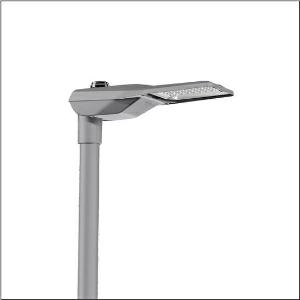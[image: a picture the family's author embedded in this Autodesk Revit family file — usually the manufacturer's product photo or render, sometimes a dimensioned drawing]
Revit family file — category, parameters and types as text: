
# Revit family: streetlight_sl_21_mini___st0_8a_5xe6c37n08gb_efcc
name_source: partatom
category: Lighting Fixtures
units: mm (PartAtom-declared; Revit-internal decimal feet)

## family parameters
Cut with Voids When Loaded = No
Host = Face
Light Source = No
Part Type = Normal
Room Calculation Point = No
Round Connector Dimension = Use Diameter
Shared = No

## types (1)
- --- (1 x LED, 5940 lm, 40.4 W, 3000K)
    Apparent Load = 40 VA
    CIE Flux Codes = 38 75 97 100 100
    Color Rendering = 70
    Color Temperature = 3000K
    Default Elevation = 1800 mm
    Description = Streetlight SL 21 mini, mast luminaire, primary light control with lens, of PMMA, primary optical cover: cover, of toughened safety glass, transparent, light distribution: ST0.8a, light emission: direct distribution, primary light characteristic: asymmetric, installation type: side-entry, LED, 3G 1.5mm², High Power LED, rated luminous flux: 5.940lm, luminous efficacy: 147lm/W, light colour: 730, colour temperature: 3000K, control gear: NEMA (7pin), control: overheat protection, pre-setting: linear dimming characteristic, constant luminous flux control, time-dependent luminous flux control, flexible luminous flux parameterisation, mains connection: 230..240V, AC, 50/60Hz, connection cable pre-assembled, cable length: 8,5m, wiring characteristics: H07RN-F, start of lifetime: 40W, end of service life: 41W, reduction: 19W, luminaire housing, of diecast aluminium (EN AC-44300), powder-coated, Siteco® metallic grey (DB 702S), corrosivity category C5 mid according to DIN EN ISO 12944, multi-level sealing system, sealing non-destructively replaceable, inclination adjustable: 0°, 5°, 10°, 15°, length: 628mm, width: 235mm, height: 110mm, spigot size: 42mm (side-entry), mounting height: 4..8m, protection rating (complete): IP66, insulation class (complete): insulation class I (protective earthing), certification: CE, ENEC, ENEC+, VDE, impact resistance: IK09, permissible operating ambient temperature for outdoor applications: -40..+50°C, standard-compliant lighting for roads and squares, packaging unit: 1 piece

Light Distribution: ST0.8a
    Height = 110 mm
    Lamp = 1 x LED
    Lamp Light Flux = 5940 lm
    Lamp Power = 40.4 W
    Lamp count = 1
    Length = 625 mm
    Luminous efficacy = 147 lm/W
    Manufacturer = Siteco
    ModVariant = No
    Model = 5XE6C37N08GB
    Number of Poles = 1
    OnlyDefault = Yes
    Power Factor = 1
    Product Name = Streetlight SL 21 mini | ST0.8a
    Product group = mast luminaire | pylon top
    ProductGroupID = 6100
    Protection Class = Protection class I
    Protection Degree = IP 66
    RLX_Detail_Level = 1
    RLX_Emergency_Light_Flux = 0 lm
    RLX_Emergency_Type = 0
    RLX_Emergency_Type_DB = No
    RlxData = <blob elided: 92049 chars, md5=d2899446>
    Socket = socket
    Standby Power = 0 W
    System Light Flux = 5940 lm
    System Power = 40 W
    Type Comments = factory setting: luminous flux: 100 % | dim-lin: 254 | 812 mA
    Type Image = l_1294379.jpg
    URL = http://relux.com
    VarID = @adj_129572
    Voltage = 0 V
    Weight = 0.00 kg
    Width = 234 mm

## geometry (parser evidence)
native form markers: Blend x4, Sweep x11
no freeform markers — native parametric forms only
